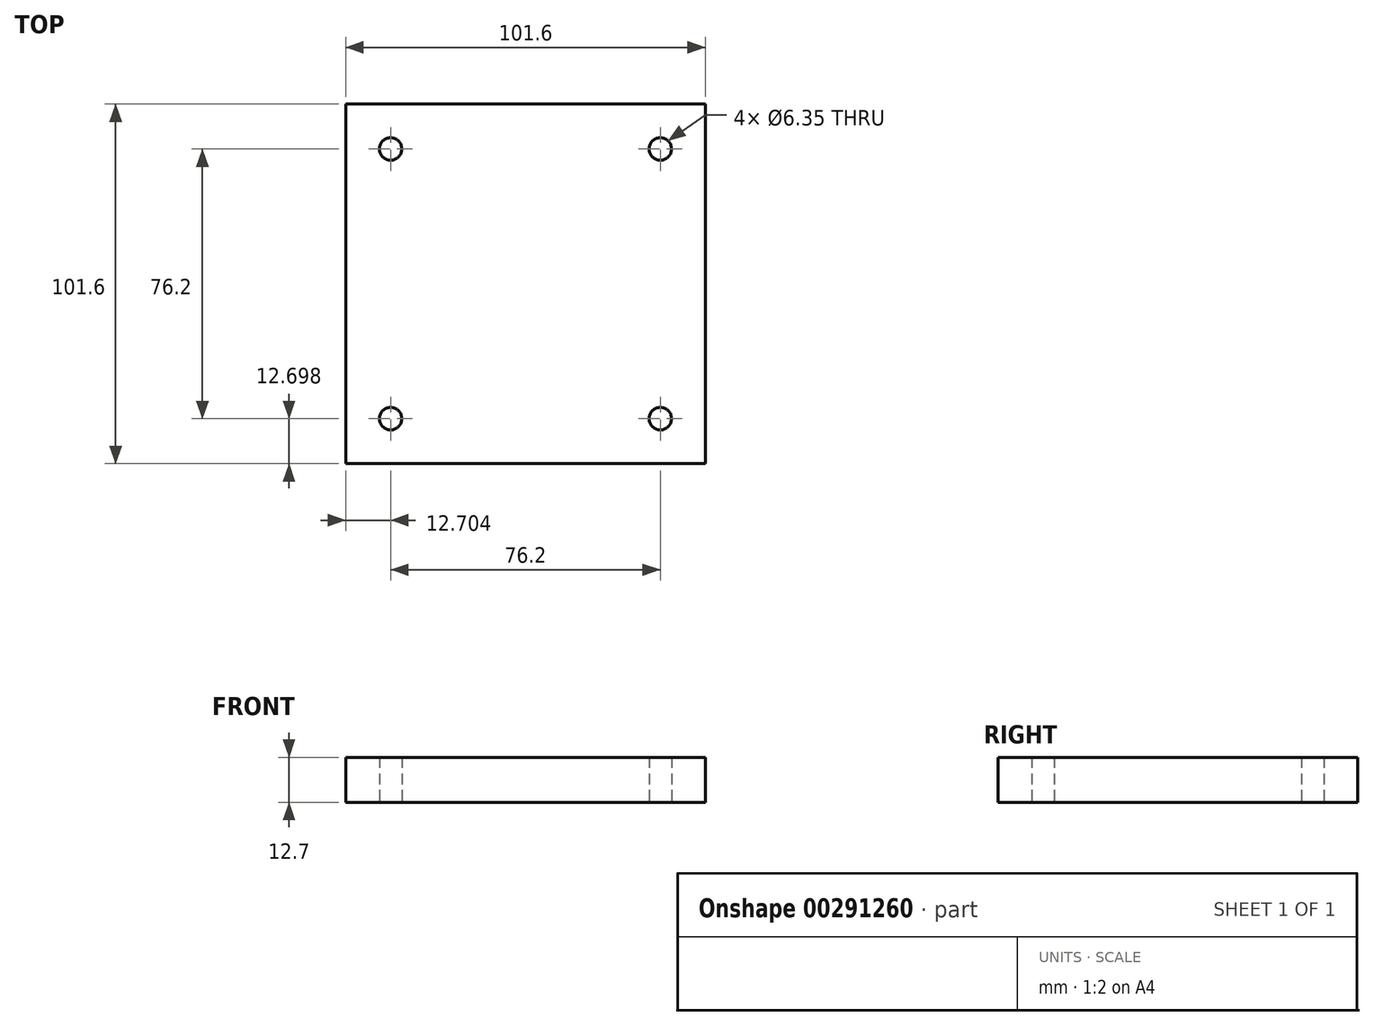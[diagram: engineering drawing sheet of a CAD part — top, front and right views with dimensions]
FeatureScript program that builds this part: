
annotation { "Feature Type Name" : "Feature", "Feature Type Description" : "" }
export const myFeature = defineFeature(function(context is Context, id is Id, definition is map)
    precondition{}
    {
        {
            var Q0;
            Q0=qCreatedBy(makeId("Top.planeOp"),FACE);
            var sketch = newSketch(context, id + "F0", { "sketchPlane" : qUnion([Q0])});
            skLineSegment(sketch, "E0.bottom", {"start": v(-51.8, 48.1) * mm, "end": v(49.8, 48.1) * mm});
            skLineSegment(sketch, "E0.top", {"start": v(-51.8, -53.5) * mm, "end": v(49.8, -53.5) * mm});
            skLineSegment(sketch, "E0.left", {"start": v(-51.8, 48.1) * mm, "end": v(-51.8, -53.5) * mm});
            skLineSegment(sketch, "E0.right", {"start": v(49.8, 48.1) * mm, "end": v(49.8, -53.5) * mm});
            skCircle(sketch, "E1", {"center": v(-39.1, 35.4) * mm, "radius": 3.18 * mm});
            skCircle(sketch, "E2", {"center": v(-39.1, -40.8) * mm, "radius": 3.18 * mm});
            skCircle(sketch, "E3", {"center": v(37.1, 35.4) * mm, "radius": 3.18 * mm});
            skCircle(sketch, "E4", {"center": v(37.1, -40.8) * mm, "radius": 3.18 * mm});
            skSolve(sketch);
        }
        {
            var Q0;
            Q0=makeQuery(id+"F0.imprint","IMPRINT",FACE,{"disambiguationData":[TD([[makeQuery(id+"F0.imprint","IMPRINT",EDGE,{"derivedFrom":sQuery(id+"F0.wireOp",EDGE,"E0.bottom")}),-1.0]])]});
            extrude(context, id + "F1", {"entities" : qUnion([Q0]), "depth" : 12.7 * mm});
        }
    });
